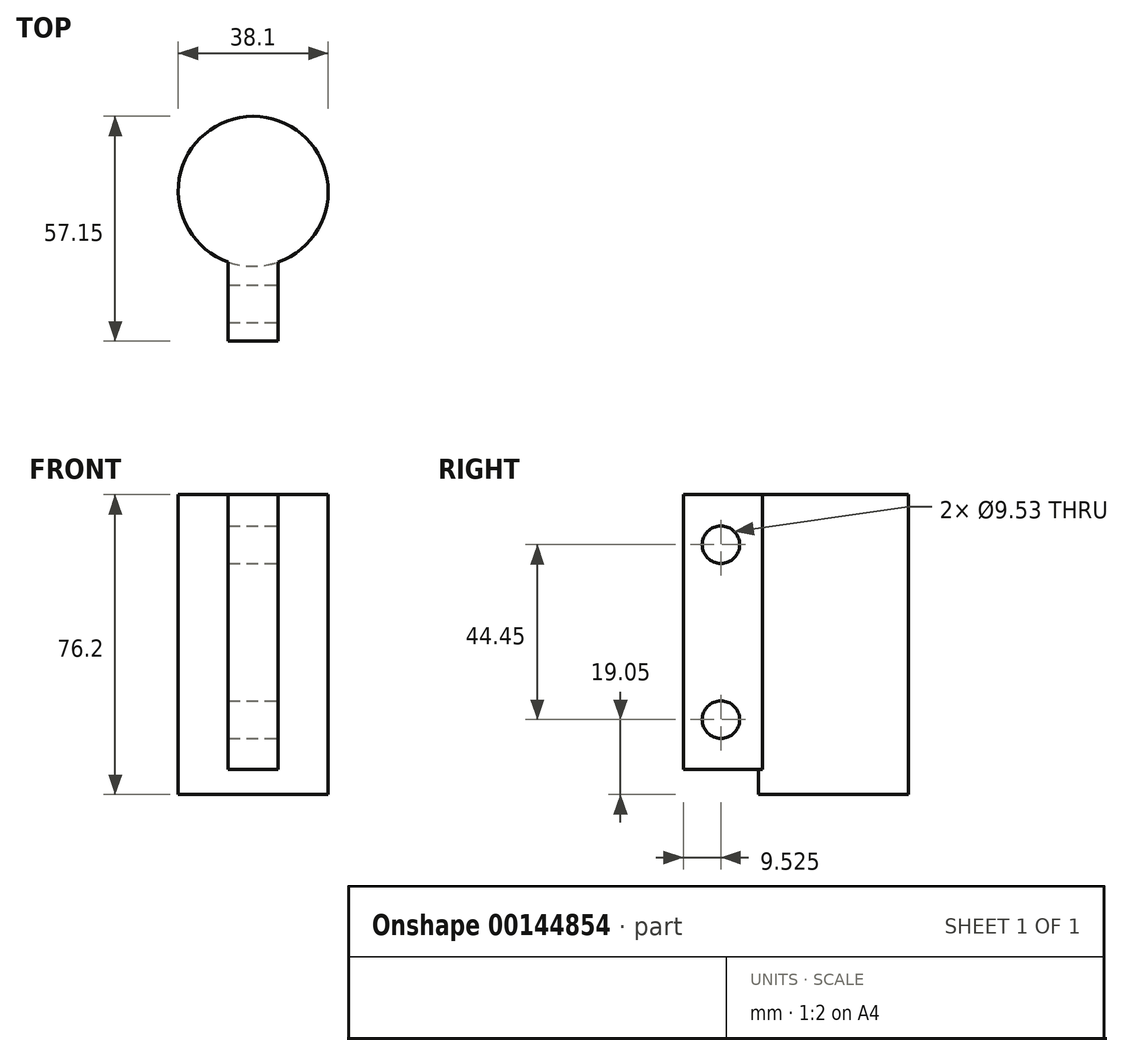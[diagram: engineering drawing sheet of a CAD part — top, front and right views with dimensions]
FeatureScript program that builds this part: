
annotation { "Feature Type Name" : "Feature", "Feature Type Description" : "" }
export const myFeature = defineFeature(function(context is Context, id is Id, definition is map)
    precondition{}
    {
        {
            var Q0;
            Q0=qCreatedBy(makeId("Top.planeOp"),FACE);
            var sketch = newSketch(context, id + "F0", { "sketchPlane" : qUnion([Q0])});
            skCircle(sketch, "E0", {"center": v(0, 0) * mm, "radius": 19.05 * mm});
            skSolve(sketch);
        }
        {
            var Q0;
            Q0=makeQuery(id+"F0.imprint","IMPRINT",FACE,{"disambiguationData":[TD([[makeQuery(id+"F0.imprint","IMPRINT",EDGE,{"derivedFrom":sQuery(id+"F0.wireOp",EDGE,"E0")}),1.0]])]});
            extrude(context, id + "F1", {"entities" : qUnion([Q0]), "depth" : 76.2 * mm});
        }
        {
            var Q0;
            Q0=qCreatedBy(makeId("Front.planeOp"),FACE);
            var sketch = newSketch(context, id + "F2", { "sketchPlane" : qUnion([Q0])});
            skLineSegment(sketch, "E1.bottom", {"start": v(6.35, 76.2) * mm, "end": v(-6.35, 76.2) * mm});
            skLineSegment(sketch, "E1.top", {"start": v(6.35, 6.35) * mm, "end": v(-6.35, 6.35) * mm});
            skLineSegment(sketch, "E1.left", {"start": v(6.35, 76.2) * mm, "end": v(6.35, 6.35) * mm});
            skLineSegment(sketch, "E1.right", {"start": v(-6.35, 76.2) * mm, "end": v(-6.35, 6.35) * mm});
            skSolve(sketch);
        }
        {
            var Q0;
            Q0 = qSketchRegion(id + "F2", true);
            extrude(context, id + "F3", {"entities" : qUnion([Q0]), "operationType" : NewBodyOperationType.ADD, "depth" : 38.1 * mm});
        }
        {
            var Q0;
            Q0=qCreatedBy(makeId("Right.planeOp"),FACE);
            var sketch = newSketch(context, id + "F4", { "sketchPlane" : qUnion([Q0])});
            skCircle(sketch, "E2", {"center": v(-28.58, 63.5) * mm, "radius": 4.76 * mm});
            skCircle(sketch, "E3", {"center": v(-28.57, 19.05) * mm, "radius": 4.76 * mm});
            skLineSegment(sketch, "E4", {"start": v(-28.58, 63.5) * mm, "end": v(-28.57, 19.05) * mm, "construction": true});
            skSolve(sketch);
        }
        {
            var Q0;
            Q0 = qSketchRegion(id + "F4", true);
            extrude(context, id + "F5", {"entities" : qUnion([Q0]), "operationType" : NewBodyOperationType.REMOVE, "endBound" : BoundingType.SYMMETRIC, "oppositeDirection" : true, "depth" : 25.4 * mm});
        }
    });
